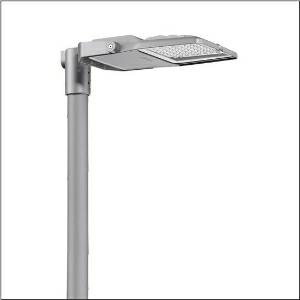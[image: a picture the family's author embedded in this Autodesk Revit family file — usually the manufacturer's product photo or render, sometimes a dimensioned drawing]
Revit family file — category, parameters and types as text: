
# Revit family: floodlight_fl_21_mini___pl64_5xa7776b4e3a_6864
name_source: partatom
category: Lighting Fixtures
units: mm (PartAtom-declared; Revit-internal decimal feet)

## family parameters
Cut with Voids When Loaded = No
Host = Face
Light Source = No
Part Type = Normal
Room Calculation Point = No
Round Connector Dimension = Use Diameter
Shared = No

## types (1)
- --- (1 x LED, 6260 lm, 45.7 W, 4000K)
    Apparent Load = 46 VA
    CIE Flux Codes = 28 80 98 100 100
    Color Rendering = 70
    Color Temperature = 4000K
    Default Elevation = 1800 mm
    Description = Floodlight FL 21 mini, floodlight, primary light control with lens, of PMMA, primary optical cover: protective disc, of toughened safety glass, transparent, light distribution: PL64, light emission: direct distribution, installation type: surface-mounted, LED, High Power LED, rated luminous flux: 6.260lm, luminous efficacy: 137lm/W, light colour: 740, colour temperature: 4000K, control gear: D4iSmart Interface (Zhaga), control: overheat protection, constant luminous flux control, time-dependent luminous flux control, flexible luminous flux parameterisation, pre-setting: logarithmic dimming characteristic, with terminal, 6-pole, mains connection: 220..240V, AC, 50/60Hz, start of lifetime: 46W, end of service life: 48W, reduction: 22W, mast bracket, of diecast aluminium, powder-coated, Siteco® metallic grey (DB 702S), corrosivity category C5 mid according to DIN EN ISO 12944, suitable for swimming pools, chlorine-resistant, sealing non-destructively replaceable, mast bracket, of steel, galvanised, powder-coated, Siteco® metallic grey (DB 702S), Smart Interface below and above, protection rating (complete): IP66, insulation class (complete): insulation class II (safety insulation), certification: CE, ENEC, VDE, protection symbol: D, impact resistance: IK08, permissible operating ambient temperature: -40..+40°C, permissible operating ambient temperature for outdoor applications: -40..+50°C, standard: DIN EN 12944, LABS conformity tested according to VDMA 24364:2018-05, packaging unit: 1 piece

Light Distribution: PL64
    Height = 70 mm
    Lamp = 1 x LED
    Lamp Light Flux = 6260 lm
    Lamp Power = 45.7 W
    Lamp count = 1
    Length = 485 mm
    Luminous efficacy = 137 lm/W
    Manufacturer = Siteco
    ModVariant = No
    Model = 5XA7776B4E3A
    Number of Poles = 1
    OnlyDefault = Yes
    Power Factor = 1
    Product Name = Floodlight FL 21 mini | PL64
    Product group = floodlight | pylon annexe
    ProductGroupID = 6200
    Protection Class = Protection class II
    Protection Degree = IP 66
    RLX_Detail_Level = 1
    RLX_Emergency_Light_Flux = 0 lm
    RLX_Emergency_Type = 0
    RLX_Emergency_Type_DB = No
    RlxData = <blob elided: 100977 chars, md5=a69a4c5f>
    Socket = socket
    Standby Power = 0 W
    System Light Flux = 6260 lm
    System Power = 46 W
    Type Comments = factory setting: luminous flux: 100 % | dim-lin: 254 | 463 mA
    Type Image = l_1007125.jpg
    URL = http://relux.com
    VarID = @adj_097120
    Voltage = 0 V
    Weight = 0.00 kg
    Width = 337 mm

## geometry (parser evidence)
native form markers: Blend x4, Sweep x12
no freeform markers — native parametric forms only
